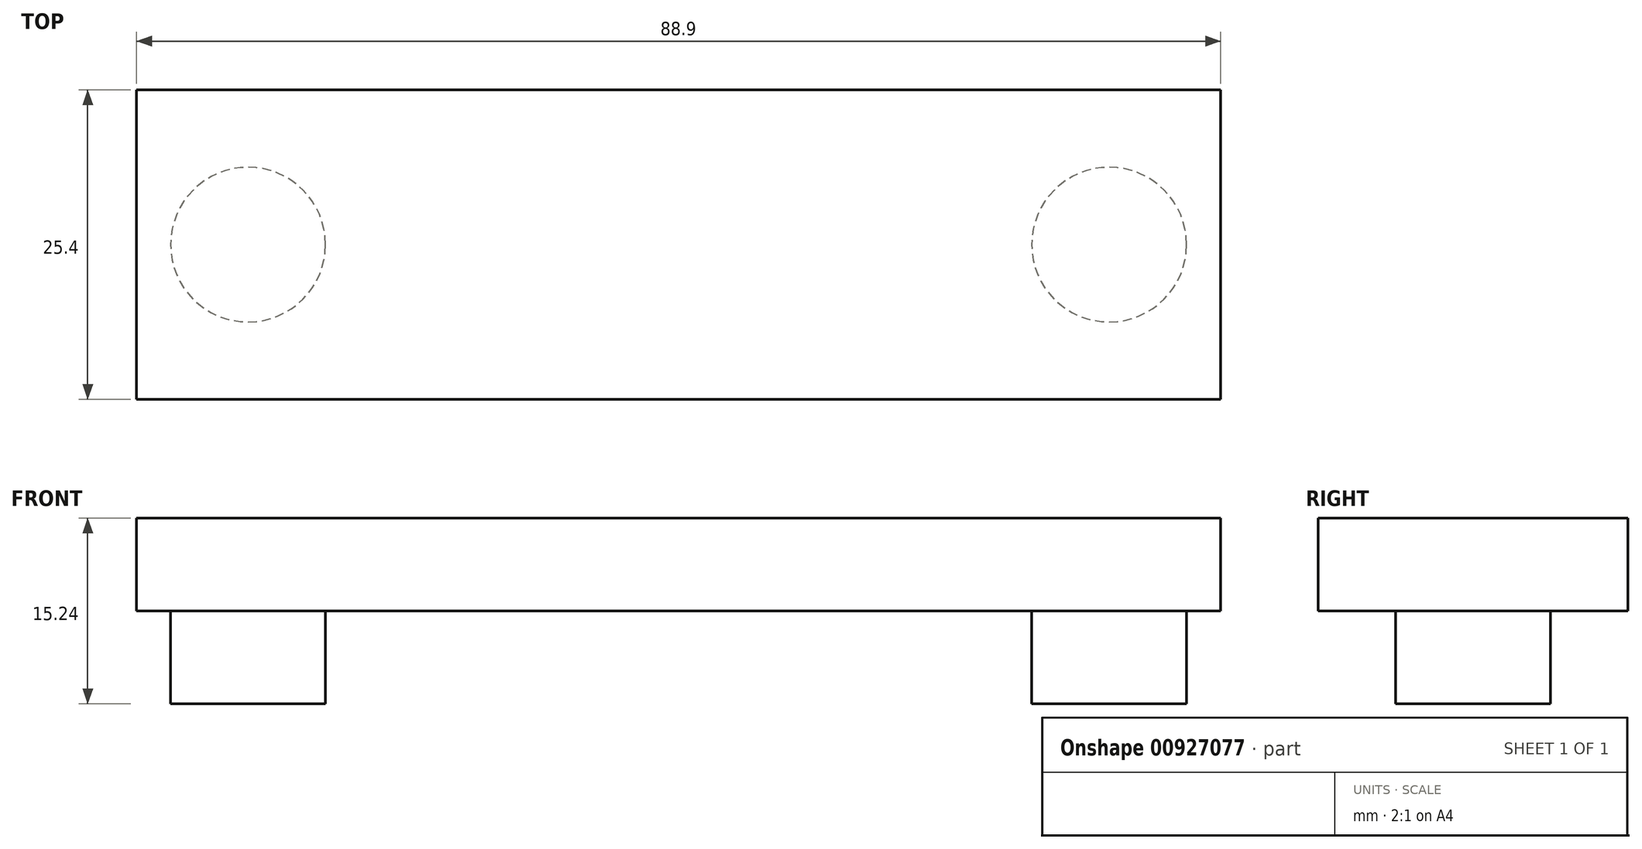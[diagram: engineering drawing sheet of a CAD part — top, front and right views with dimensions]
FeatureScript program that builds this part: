
annotation { "Feature Type Name" : "Feature", "Feature Type Description" : "" }
export const myFeature = defineFeature(function(context is Context, id is Id, definition is map)
    precondition{}
    {
        {
            var Q0;
            Q0=qCreatedBy(makeId("Top.planeOp"),FACE);
            var sketch = newSketch(context, id + "F0", { "sketchPlane" : qUnion([Q0])});
            skLineSegment(sketch, "E0.bottom", {"start": v(44.45, 12.7) * mm, "end": v(-44.45, 12.7) * mm});
            skLineSegment(sketch, "E0.top", {"start": v(44.45, -12.7) * mm, "end": v(-44.45, -12.7) * mm});
            skLineSegment(sketch, "E0.left", {"start": v(44.45, 12.7) * mm, "end": v(44.45, -12.7) * mm});
            skLineSegment(sketch, "E0.right", {"start": v(-44.45, 12.7) * mm, "end": v(-44.45, -12.7) * mm});
            skPoint(sketch, "E0.middle", {"position": v(0, 0) * mm});
            skSolve(sketch);
        }
        {
            var Q0;
            Q0=makeQuery(id+"F0.imprint","IMPRINT",FACE,{"disambiguationData":[TD([[makeQuery(id+"F0.imprint","IMPRINT",EDGE,{"derivedFrom":sQuery(id+"F0.wireOp",EDGE,"E0.bottom")}),1.0]])]});
            extrude(context, id + "F1", {"entities" : qUnion([Q0]), "endBound" : BoundingType.SYMMETRIC, "depth" : 7.62 * mm, "offsetDistance" : 25.4 * mm});
        }
        {
            var Q0;
            Q0=qCreatedBy(makeId("Top.planeOp"),FACE);
            cPlane(context, id + "F2", {"entities" : qUnion([Q0]), "cplaneType" : CPlaneType.OFFSET, "offset" : 3.8 * mm, "oppositeDirection" : true, "width" : 152.4 * mm, "height" : 152.4 * mm});
        }
        {
            var Q0;
            Q0=qCreatedBy(id+"F2.planeOp",FACE);
            var sketch = newSketch(context, id + "F3", { "sketchPlane" : qUnion([Q0])});
            skCircle(sketch, "E1", {"center": v(-35.3, 0) * mm, "radius": 6.35 * mm});
            skCircle(sketch, "E2", {"center": v(35.3, 0) * mm, "radius": 6.35 * mm});
            skSolve(sketch);
        }
        {
            var Q0;
            Q0=makeQuery(id+"F3.imprint","IMPRINT",FACE,{"disambiguationData":[TD([[makeQuery(id+"F3.imprint","IMPRINT",EDGE,{"derivedFrom":sQuery(id+"F3.wireOp",EDGE,"E1")}),1.0]])]});
            var Q1;
            Q1=makeQuery(id+"F3.imprint","IMPRINT",FACE,{"disambiguationData":[TD([[makeQuery(id+"F3.imprint","IMPRINT",EDGE,{"derivedFrom":sQuery(id+"F3.wireOp",EDGE,"E2")}),1.0]])]});
            extrude(context, id + "F4", {"entities" : qUnion([Q0, Q1]), "operationType" : NewBodyOperationType.ADD, "oppositeDirection" : true, "depth" : 7.62 * mm, "offsetDistance" : 25.4 * mm});
        }
    });
